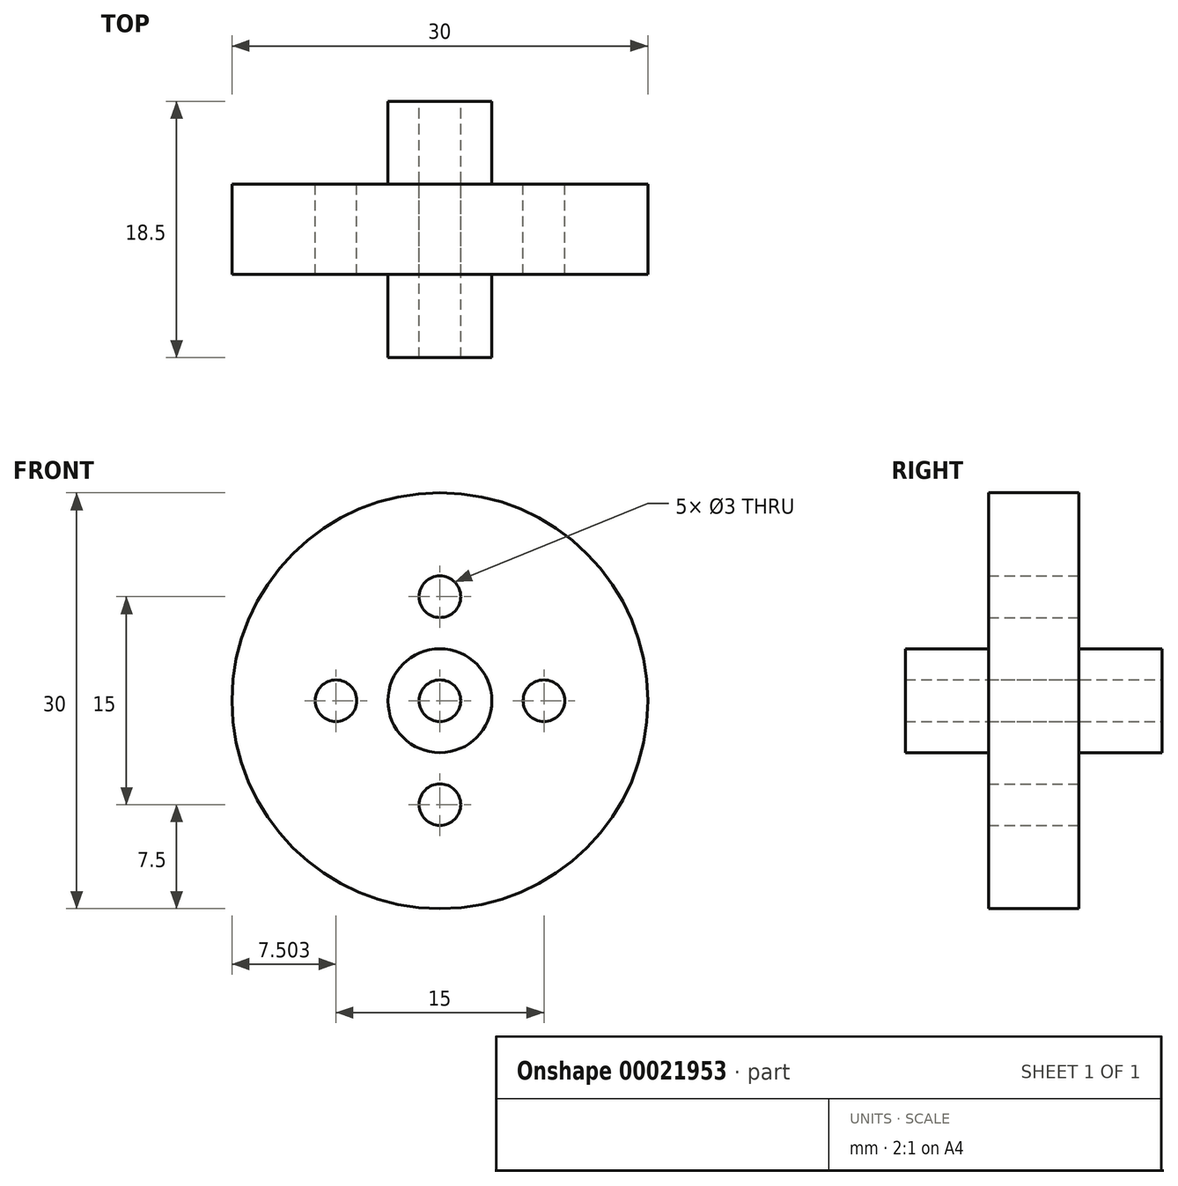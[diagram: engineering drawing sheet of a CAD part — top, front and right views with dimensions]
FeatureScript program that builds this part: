
annotation { "Feature Type Name" : "Feature", "Feature Type Description" : "" }
export const myFeature = defineFeature(function(context is Context, id is Id, definition is map)
    precondition{}
    {
        {
            var Q0;
            Q0=qCreatedBy(makeId("Front.planeOp"),FACE);
            var sketch = newSketch(context, id + "F0", { "sketchPlane" : qUnion([Q0])});
            skCircle(sketch, "E0", {"center": v(36.65, 26.67) * mm, "radius": 15 * mm});
            skCircle(sketch, "E1", {"center": v(36.65, 26.67) * mm, "radius": 1.5 * mm});
            skCircle(sketch, "E2", {"center": v(36.65, 26.67) * mm, "radius": 3.75 * mm});
            skLineSegment(sketch, "E3", {"start": v(36.65, 28.17) * mm, "end": v(36.65, 34.17) * mm});
            skCircle(sketch, "E4", {"center": v(36.65, 34.17) * mm, "radius": 1.5 * mm});
            skCircle(sketch, "E5.1.0", {"center": v(29.15, 26.67) * mm, "radius": 1.5 * mm});
            skCircle(sketch, "E5.2.0", {"center": v(36.65, 19.17) * mm, "radius": 1.5 * mm});
            skCircle(sketch, "E5.3.0", {"center": v(44.15, 26.67) * mm, "radius": 1.5 * mm});
            skSolve(sketch);
        }
        {
            var Q0;
            Q0=qSketchRegion(id+"F0",true);
            var Q1;
            Q1=makeQuery(id+"F0.imprint","IMPRINT",FACE,{"disambiguationData":[TD([[makeQuery(id+"F0.imprint","IMPRINT",EDGE,{"derivedFrom":sQuery(id+"F0.wireOp",EDGE,"E0")}),1.0]])]});
            extrude(context, id + "F1", {"entities" : qUnion([Q0, Q1]), "depth" : 6.5 * mm});
        }
        {
            var Q0;
            Q0=makeQuery(id+"F0.imprint","IMPRINT",FACE,{"disambiguationData":[TD([[makeQuery(id+"F0.imprint","IMPRINT",EDGE,{"derivedFrom":sQuery(id+"F0.wireOp",EDGE,"E1")}),-1.0]])]});
            extrude(context, id + "F2", {"entities" : qUnion([Q0]), "operationType" : NewBodyOperationType.ADD, "depth" : 12.5 * mm});
        }
        {
            var Q0;
            Q0=makeQuery(id+"F0.imprint","IMPRINT",FACE,{"disambiguationData":[TD([[makeQuery(id+"F0.imprint","IMPRINT",EDGE,{"derivedFrom":sQuery(id+"F0.wireOp",EDGE,"E1")}),-1.0]])]});
            extrude(context, id + "F3", {"entities" : qUnion([Q0]), "operationType" : NewBodyOperationType.ADD, "oppositeDirection" : true, "depth" : 6 * mm});
        }
    });
